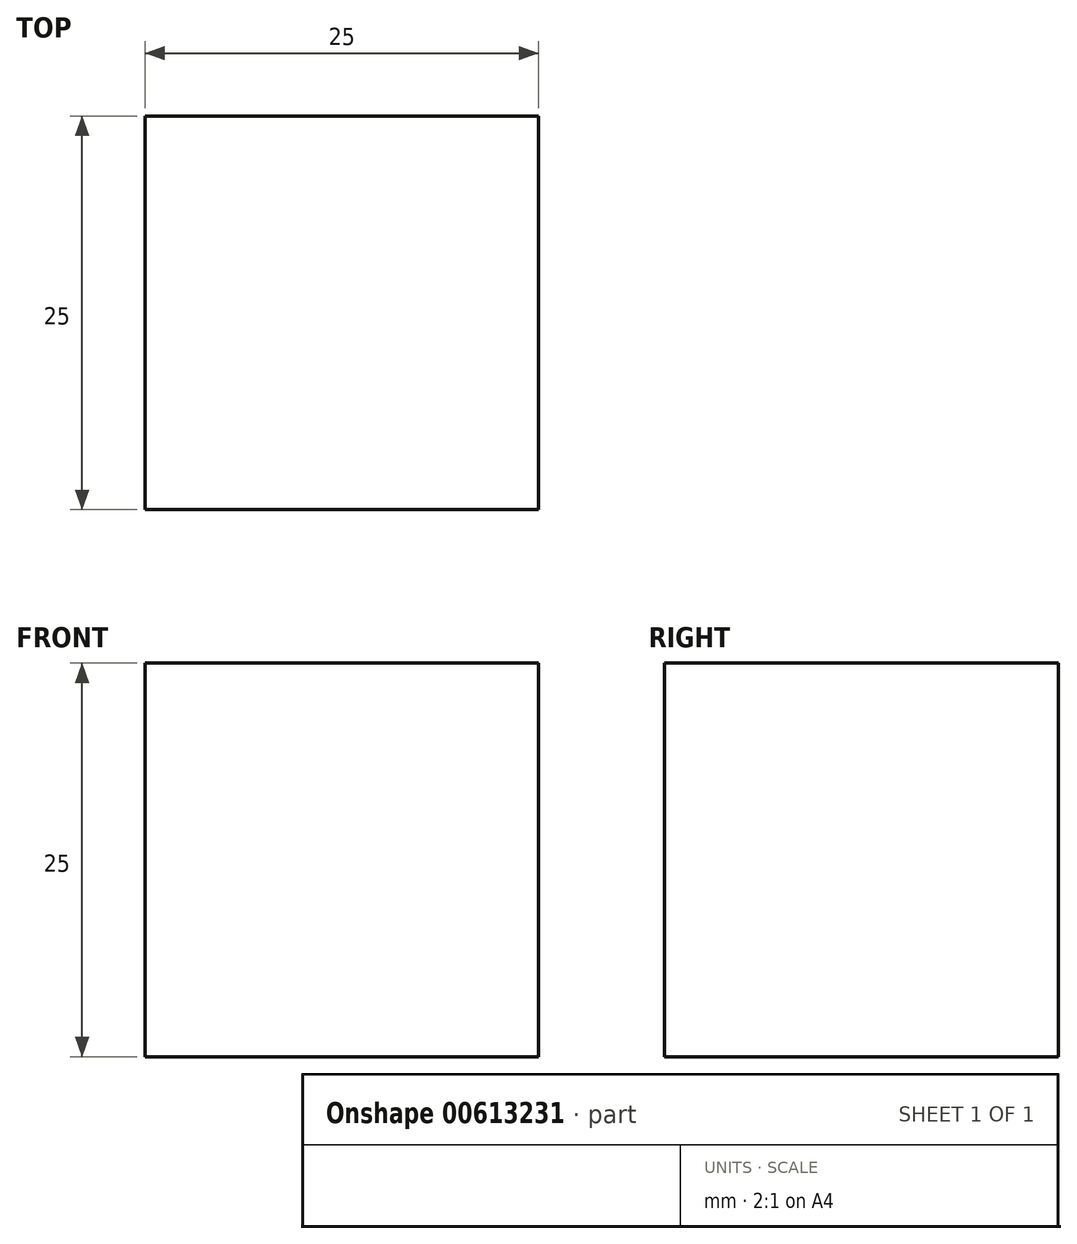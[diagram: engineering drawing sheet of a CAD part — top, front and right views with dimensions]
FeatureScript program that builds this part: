
annotation { "Feature Type Name" : "Feature", "Feature Type Description" : "" }
export const myFeature = defineFeature(function(context is Context, id is Id, definition is map)
    precondition{}
    {
        {
            var Q0;
            Q0=qCreatedBy(makeId("Front.planeOp"),FACE);
            var sketch = newSketch(context, id + "F0", { "sketchPlane" : qUnion([Q0])});
            skLineSegment(sketch, "E0.bottom", {"start": v(12.5, 12.5) * mm, "end": v(-12.5, 12.5) * mm});
            skLineSegment(sketch, "E0.top", {"start": v(12.5, -12.5) * mm, "end": v(-12.5, -12.5) * mm});
            skLineSegment(sketch, "E0.left", {"start": v(12.5, 12.5) * mm, "end": v(12.5, -12.5) * mm});
            skLineSegment(sketch, "E0.right", {"start": v(-12.5, 12.5) * mm, "end": v(-12.5, -12.5) * mm});
            skSolve(sketch);
        }
        {
            var Q0;
            Q0=makeQuery(id+"F0.imprint","IMPRINT",FACE,{"disambiguationData":[TD([[makeQuery(id+"F0.imprint","IMPRINT",EDGE,{"derivedFrom":sQuery(id+"F0.wireOp",EDGE,"E0.bottom")}),1.0]])]});
            extrude(context, id + "F1", {"entities" : qUnion([Q0]), "depth" : 25 * mm, "offsetDistance" : 25 * mm});
        }
    });
